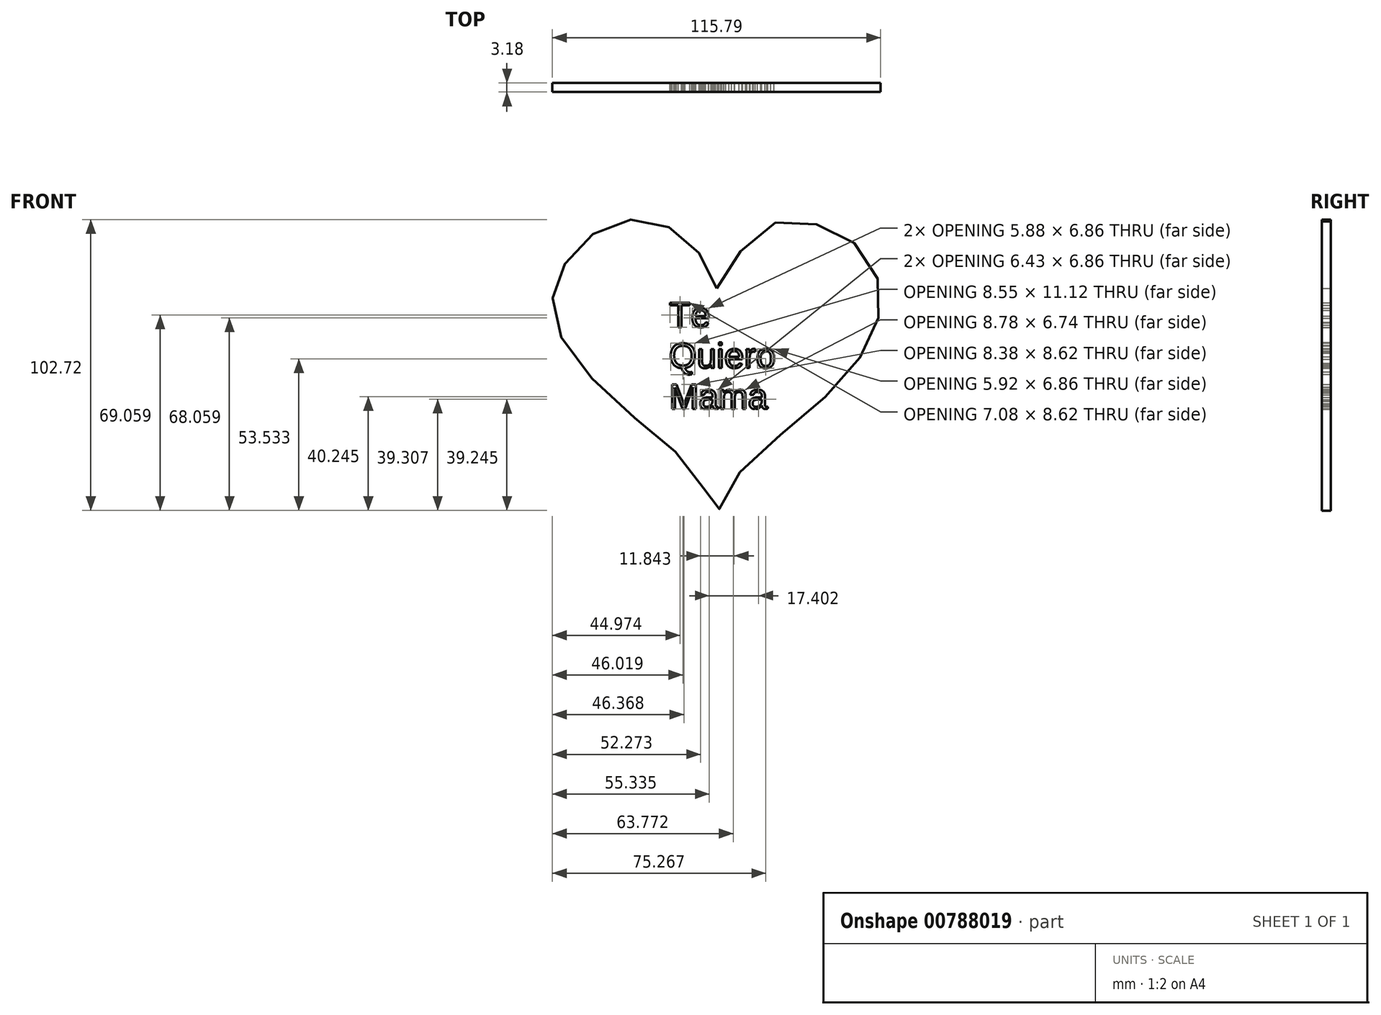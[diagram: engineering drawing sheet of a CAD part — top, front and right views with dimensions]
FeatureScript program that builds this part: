
annotation { "Feature Type Name" : "Feature", "Feature Type Description" : "" }
export const myFeature = defineFeature(function(context is Context, id is Id, definition is map)
    precondition{}
    {
        {
            var Q0;
            Q0=qCreatedBy(makeId("Front.planeOp"),FACE);
            var sketch = newSketch(context, id + "F0", { "sketchPlane" : qUnion([Q0])});
            skFitSpline(sketch, "E0", {"points": [v(0, 26.11) * mm, v(-7.48, 40.77) * mm, v(-19.7, 48.4) * mm, v(-34.36, 49.93) * mm, v(-49.01, 40.46) * mm, v(-56.65, 28.55) * mm, v(-57.26, 14.81) * mm, v(-45.35, -4.43) * mm, v(-21.22, -26.11) * mm, v(-5.95, -41.99) * mm, v(0, -52.37) * mm, v(5.95, -41.99) * mm, v(27.64, -21.53) * mm, v(49.32, 0) * mm, v(57.26, 16.95) * mm, v(55.73, 32.22) * mm, v(43.52, 45.65) * mm, v(27.03, 49.62) * mm, v(11.76, 44.13) * mm, v(0, 26.11) * mm]});
            skSolve(sketch);
        }
        {
            var Q0;
            Q0=makeQuery(id+"F0.imprint","IMPRINT",FACE,{"disambiguationData":[TD([[makeQuery(id+"F0.imprint","IMPRINT",EDGE,{"derivedFrom":sQuery(id+"F0.wireOp",EDGE,"E0")}),1.0]])]});
            extrude(context, id + "F1", {"entities" : qUnion([Q0]), "depth" : 3.17 * mm, "offsetDistance" : 25.4 * mm});
        }
        {
            var Q0;
            Q0=qCreatedBy(makeId("Front.planeOp"),FACE);
            var sketch = newSketch(context, id + "F2", { "sketchPlane" : qUnion([Q0])});
            skText(sketch, "E1", { "text": "Te \nQuiero\nMama", "fontName": "Arimo-Regular.ttf"});
            const initialGuessF2  = {"E1": [-0.01686, 0.01238, 1, 0, 0.00902]};
            skSetInitialGuess(sketch, initialGuessF2);
            skSolve(sketch);
        }
        {
            var Q0;
            Q0 = qSketchRegion(id + "F2", true);
            extrude(context, id + "F3", {"entities" : qUnion([Q0]), "operationType" : NewBodyOperationType.REMOVE, "endBound" : BoundingType.THROUGH_ALL, "depth" : 25.4 * mm, "offsetDistance" : 25.4 * mm});
        }
    });
